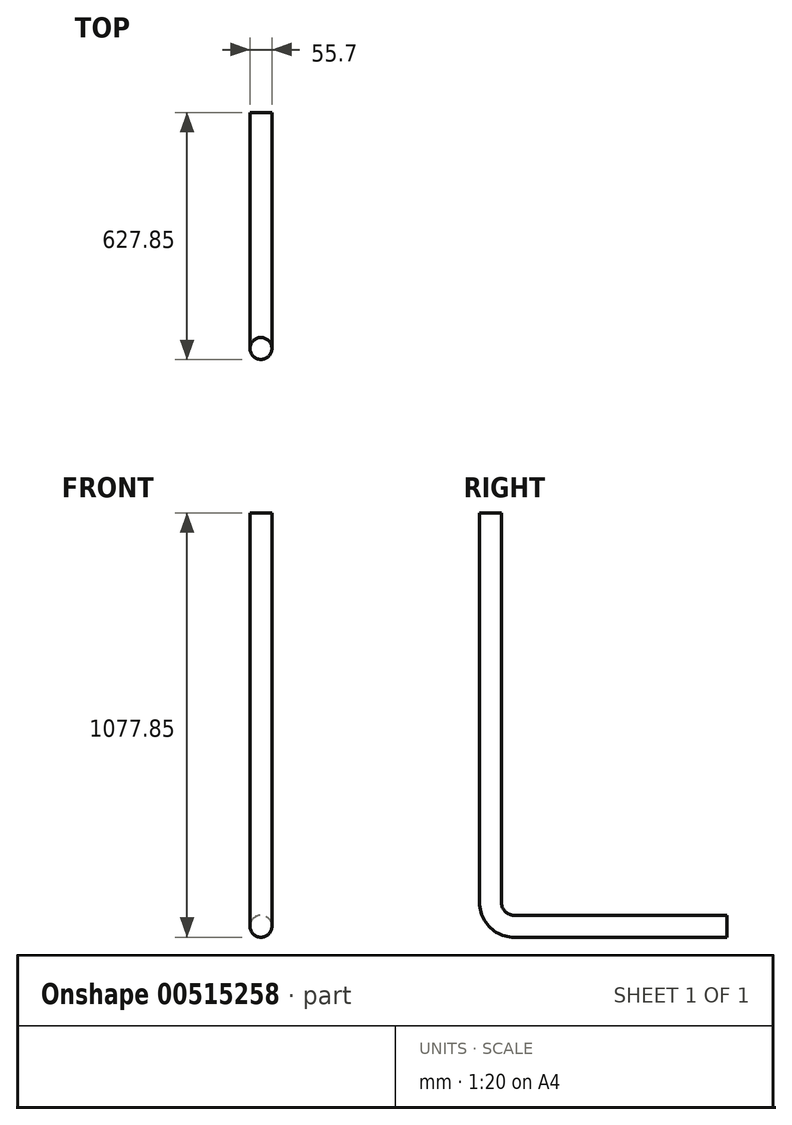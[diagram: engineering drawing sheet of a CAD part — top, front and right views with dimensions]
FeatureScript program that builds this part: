
annotation { "Feature Type Name" : "Feature", "Feature Type Description" : "" }
export const myFeature = defineFeature(function(context is Context, id is Id, definition is map)
    precondition{}
    {
        {
            var Q0;
            Q0=qCreatedBy(makeId("Right.planeOp"),FACE);
            var sketch = newSketch(context, id + "F0", { "sketchPlane" : qUnion([Q0])});
            skLineSegment(sketch, "E0", {"start": v(0, 60) * mm, "end": v(0, 1050) * mm});
            skLineSegment(sketch, "E1", {"start": v(60, 0) * mm, "end": v(600, 0) * mm});
            skPoint(sketch, "E2.visualSharp", {"position": v(0, 0) * mm});
            skArc(sketch, "E2.filletArc", {"start": v(0, 60) * mm, "mid": v(17.57, 17.57) * mm, "end": v(60, 0) * mm});
            skSolve(sketch);
        }
        {
            var Q0;
            Q0=sQuery(id+"F0.wireOp",VERTEX,"E0.end");
            var Q1;
            Q1=qCreatedBy(makeId("Top.planeOp"),FACE);
            cPlane(context, id + "F1", {"entities" : qUnion([Q0, Q1]), "cplaneType" : CPlaneType.PLANE_POINT, "offset" : 25 * mm, "width" : 150 * mm, "height" : 150 * mm});
        }
        {
            var Q0;
            Q0=qCreatedBy(id+"F1.planeOp",FACE);
            var sketch = newSketch(context, id + "F2", { "sketchPlane" : qUnion([Q0])});
            skCircle(sketch, "E3", {"center": v(0, 0) * mm, "radius": 27.85 * mm});
            skSolve(sketch);
        }
        {
            var Q0;
            Q0=makeQuery(id+"F2.imprint","IMPRINT",FACE,{"disambiguationData":[TD([[makeQuery(id+"F2.imprint","IMPRINT",EDGE,{"derivedFrom":sQuery(id+"F2.wireOp",EDGE,"E3")}),1.0]])]});
            var Q1;
            Q1=sQuery(id+"F0.wireOp",EDGE,"E0");
            var Q2;
            Q2=sQuery(id+"F0.wireOp",EDGE,"E2.filletArc");
            var Q3;
            Q3=sQuery(id+"F0.wireOp",EDGE,"E1");
            sweep(context, id + "F3", {"profiles" : qUnion([Q0]), "path" : qUnion([Q1, Q2, Q3])});
        }
    });
